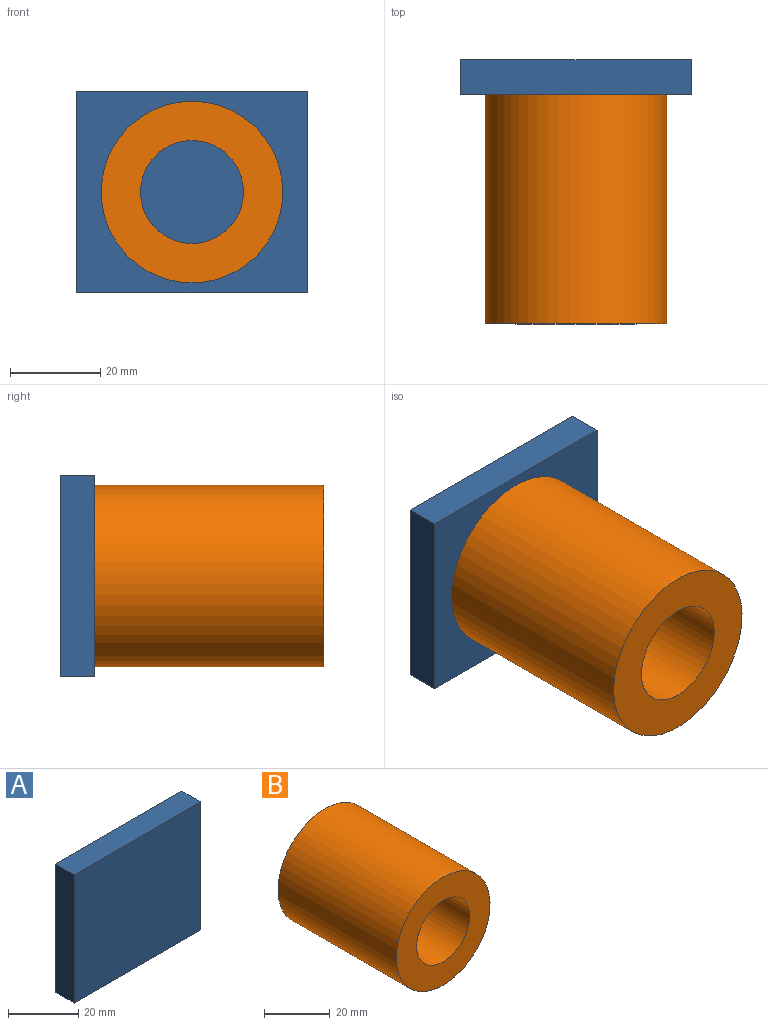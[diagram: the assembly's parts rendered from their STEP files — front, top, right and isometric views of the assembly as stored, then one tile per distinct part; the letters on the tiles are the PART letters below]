
ASSEMBLY  parts=2 mates=1
PART A: 6 faces, bbox 51x7.6x44.7 mm
  f0: plane 50.96x7.62mm, normal (0,0,-1), area 388.3mm2, adj f1,f3,f4,f5
  f1: plane 44.69x7.62mm, normal (1,0,0), area 340.5mm2, adj f0,f2,f4,f5
  f2: plane 50.96x7.62mm, normal (0,0,1), area 388.3mm2, adj f1,f3,f4,f5
  f3: plane 44.69x7.62mm, normal (-1,0,0), area 340.5mm2, adj f0,f2,f4,f5
  f4: plane 50.96x44.69mm, normal (0,-1,0), area 2277.3mm2, adj f0,f1,f2,f3
  f5: plane 50.96x44.69mm, normal (0,1,0), area 2277.3mm2, adj f0,f1,f2,f3
PART B: 4 faces, bbox 40.2x50.8x40.2 mm
  f0: cylinder r=11.39mm len=50.8mm, axis (0,1,0), area 3636.7mm2, adj f2,f3
  f1: cylinder r=20.11mm len=50.8mm, axis (0,1,0), area 6417.9mm2, adj f2,f3
  f2: plane 40.21x40.21mm, normal (0,-1,0), area 862.3mm2, adj f0,f1
  f3: plane 40.21x40.21mm, normal (0,1,0), area 862.3mm2, adj f0,f1
PLACE A t=(54.16,14.48,-44.43)mm
PLACE B t=(10.41,6.86,1.27)mm
MATE fastened A.f4 <-> B.f0  axis (0,-1,0) through (10.41,6.86,1.27)mm
